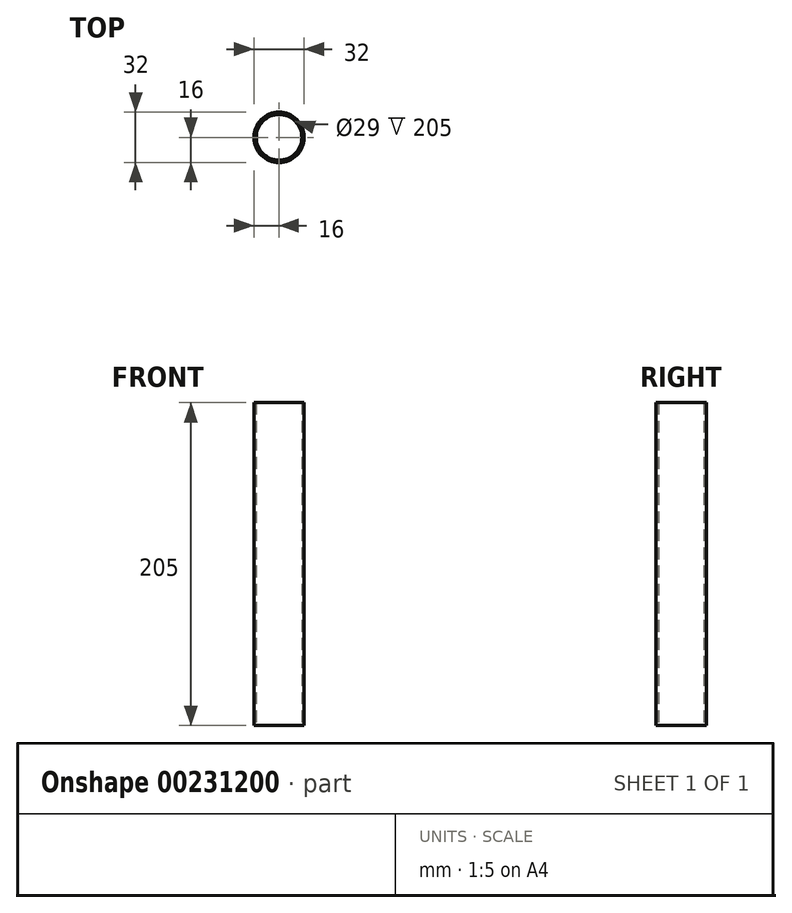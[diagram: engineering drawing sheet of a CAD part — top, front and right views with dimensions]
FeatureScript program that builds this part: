
annotation { "Feature Type Name" : "Feature", "Feature Type Description" : "" }
export const myFeature = defineFeature(function(context is Context, id is Id, definition is map)
    precondition{}
    {
        {
            var Q0;
            Q0=qCreatedBy(makeId("Top.planeOp"),FACE);
            var sketch = newSketch(context, id + "F0", { "sketchPlane" : qUnion([Q0])});
            skCircle(sketch, "E0", {"center": v(0, 0) * mm, "radius": 16 * mm});
            skCircle(sketch, "E1", {"center": v(0, 0) * mm, "radius": 14.5 * mm});
            skSolve(sketch);
        }
        {
            var Q0;
            Q0=makeQuery(id+"F0.imprint","IMPRINT",FACE,{"disambiguationData":[TD([[makeQuery(id+"F0.imprint","IMPRINT",EDGE,{"derivedFrom":sQuery(id+"F0.wireOp",EDGE,"E0")}),1.0]])]});
            extrude(context, id + "F1", {"entities" : qUnion([Q0]), "depth" : 205 * mm});
        }
    });
